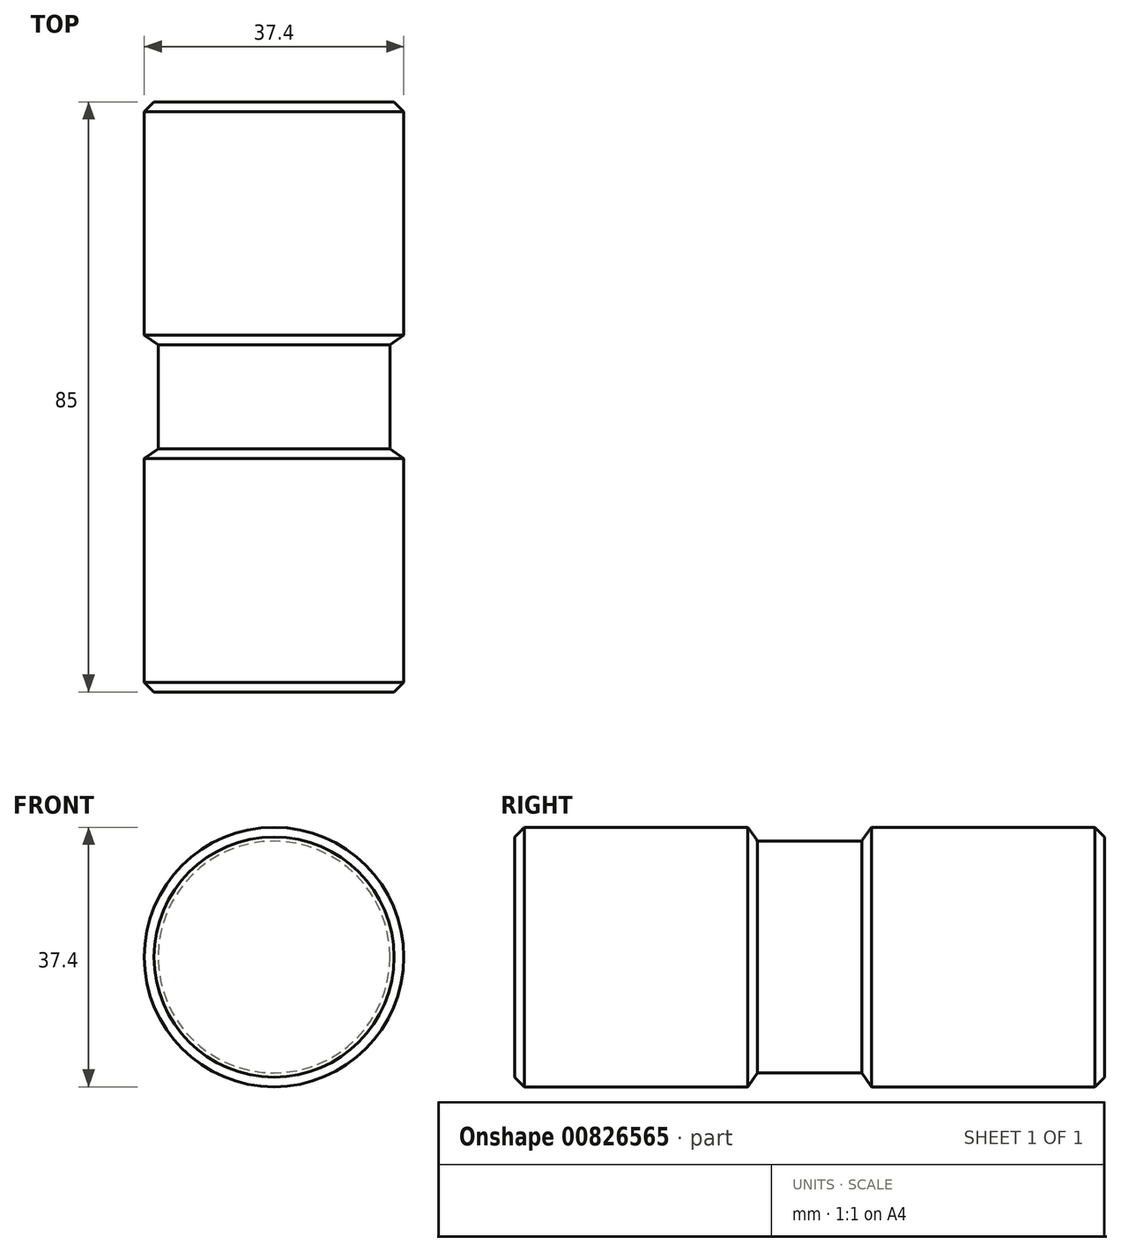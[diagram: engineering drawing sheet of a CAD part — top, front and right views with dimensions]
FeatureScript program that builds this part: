
annotation { "Feature Type Name" : "Feature", "Feature Type Description" : "" }
export const myFeature = defineFeature(function(context is Context, id is Id, definition is map)
    precondition{}
    {
        {
            var Q0;
            Q0=qCreatedBy(makeId("Top.planeOp"),FACE);
            var sketch = newSketch(context, id + "F0", { "sketchPlane" : qUnion([Q0])});
            skLineSegment(sketch, "E0", {"start": v(0, 67.95) * mm, "end": v(0, -67.95) * mm, "construction": true});
            skLineSegment(sketch, "E1.bottom", {"start": v(0, 42.5) * mm, "end": v(-18.7, 42.5) * mm});
            skLineSegment(sketch, "E1.top", {"start": v(0, -42.5) * mm, "end": v(-18.7, -42.5) * mm});
            skLineSegment(sketch, "E1.left", {"start": v(0, 42.5) * mm, "end": v(0, -42.5) * mm});
            skLineSegment(sketch, "E1.right", {"start": v(-18.7, 42.5) * mm, "end": v(-18.7, 8.9) * mm});
            skLineSegment(sketch, "E2", {"start": v(-16.7, -7.5) * mm, "end": v(-18.7, -8.9) * mm});
            skLineSegment(sketch, "E3", {"start": v(-16.7, -7.5) * mm, "end": v(-16.7, 7.5) * mm});
            skLineSegment(sketch, "E4", {"start": v(-18.7, 8.9) * mm, "end": v(-16.7, 7.5) * mm});
            skPoint(sketch, "E5", {"position": v(-16.7, 0) * mm});
            skLineSegment(sketch, "E6", {"start": v(-18.7, 8.9) * mm, "end": v(-18.7, -8.9) * mm, "construction": true});
            skLineSegment(sketch, "E7", {"start": v(-18.7, -8.9) * mm, "end": v(-18.7, -42.5) * mm});
            skSolve(sketch);
        }
        {
            var Q0;
            Q0 = qSketchRegion(id + "F0", true);
            var Q1;
            Q1=sQuery(id+"F0.wireOp",EDGE,"E0");
            revolve(context, id + "F1", {"surfaceOperationType" : NewSurfaceOperationType.NEW, "entities" : qUnion([Q0]), "axis" : qUnion([Q1]), "revolveType" : RevolveType.FULL});
        }
        {
            var Q0;
            Q0=makeQuery(id+"F1.opRevolve","SWEPT_EDGE",EDGE,{"disambiguationData":[OSD([sQuery(id+"F0.wireOp",EDGE,"E1.bottom"),sQuery(id+"F0.wireOp",EDGE,"E1.right")])]});
            var Q1;
            Q1=makeQuery(id+"F1.opRevolve","SWEPT_EDGE",EDGE,{"disambiguationData":[OSD([sQuery(id+"F0.wireOp",EDGE,"E1.top"),sQuery(id+"F0.wireOp",EDGE,"E7")])]});
            chamfer(context, id + "F2", {"entities" : qUnion([Q0, Q1]), "width" : 1.4 * mm, "tangentPropagation" : true});
        }
    });
